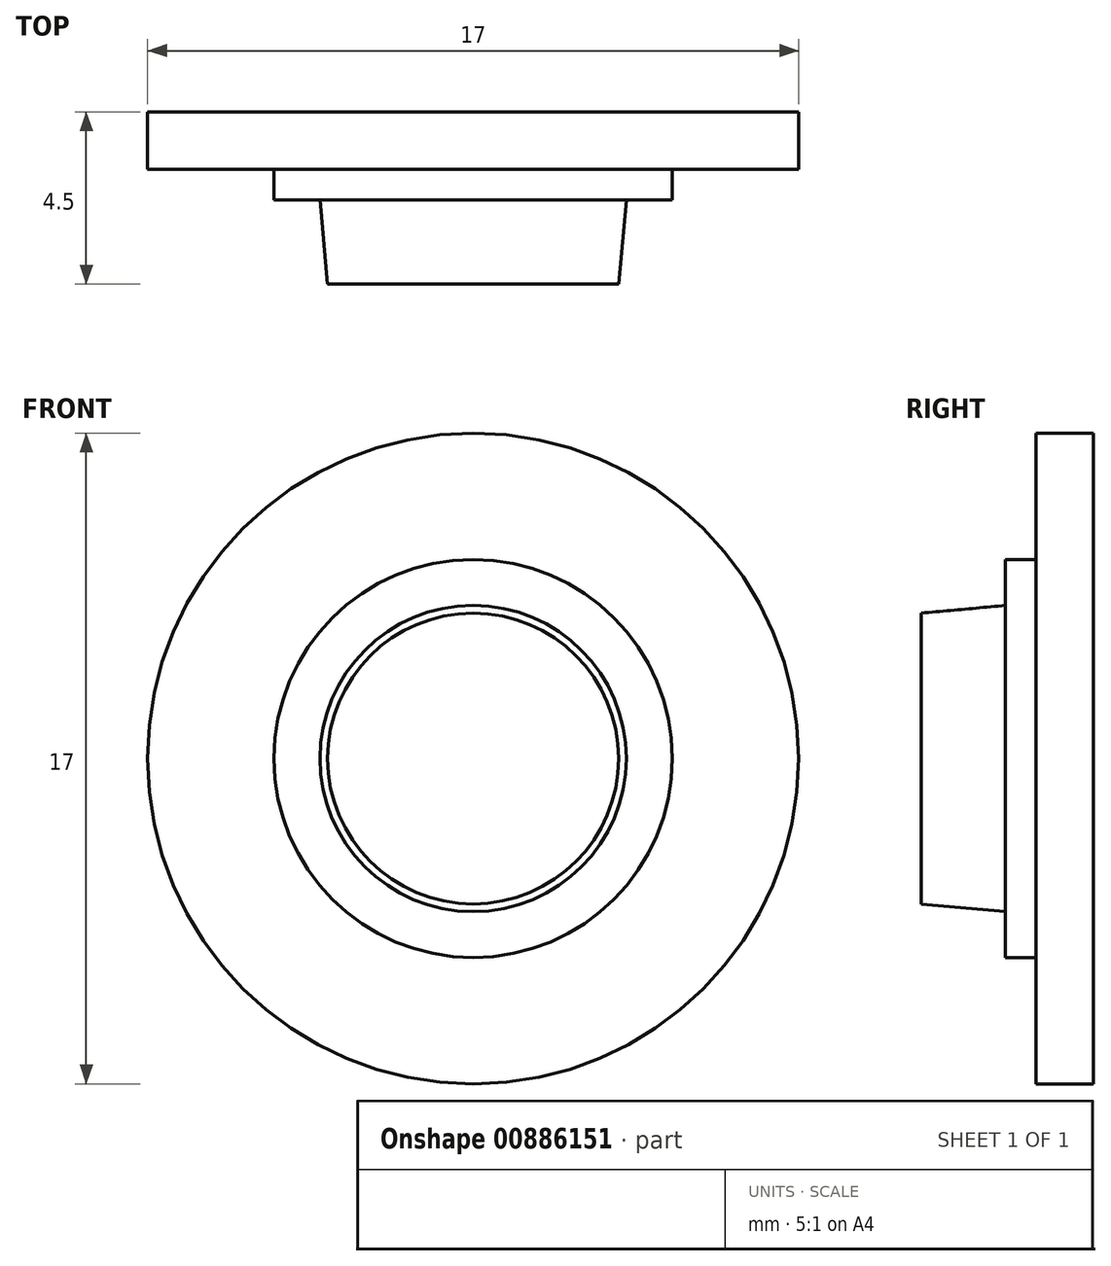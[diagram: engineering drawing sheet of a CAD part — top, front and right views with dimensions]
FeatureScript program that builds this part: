
annotation { "Feature Type Name" : "Feature", "Feature Type Description" : "" }
export const myFeature = defineFeature(function(context is Context, id is Id, definition is map)
    precondition{}
    {
        {
            var Q0;
            Q0=qCreatedBy(makeId("Top.planeOp"),FACE);
            var sketch = newSketch(context, id + "F0", { "sketchPlane" : qUnion([Q0])});
            skLineSegment(sketch, "E0", {"start": v(0, -3) * mm, "end": v(-3.8, -3) * mm});
            skLineSegment(sketch, "E1", {"start": v(-3.8, -3) * mm, "end": v(-4, -0.8) * mm});
            skLineSegment(sketch, "E2", {"start": v(-4, -0.8) * mm, "end": v(-5.2, -0.8) * mm});
            skLineSegment(sketch, "E3", {"start": v(-5.2, -0.8) * mm, "end": v(-5.2, 0) * mm});
            skLineSegment(sketch, "E4", {"start": v(-5.2, 0) * mm, "end": v(-8.5, 0) * mm});
            skLineSegment(sketch, "E5", {"start": v(-8.5, 0) * mm, "end": v(-8.5, 1.5) * mm});
            skLineSegment(sketch, "E6", {"start": v(0, 1.5) * mm, "end": v(0, -3) * mm});
            skLineSegment(sketch, "E7", {"start": v(-8.5, 1.5) * mm, "end": v(0, 1.5) * mm});
            skSolve(sketch);
        }
        {
            var Q0;
            Q0=makeQuery(id+"F0.imprint","IMPRINT",FACE,{"disambiguationData":[TD([[makeQuery(id+"F0.imprint","IMPRINT",EDGE,{"derivedFrom":sQuery(id+"F0.wireOp",EDGE,"E0")}),-1.0]])]});
            var Q1;
            Q1=sQuery(id+"F0.wireOp",EDGE,"E6");
            revolve(context, id + "F1", {"surfaceOperationType" : NewSurfaceOperationType.NEW, "entities" : qUnion([Q0]), "axis" : qUnion([Q1]), "revolveType" : RevolveType.FULL});
        }
    });
